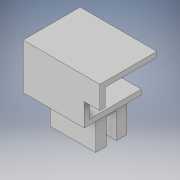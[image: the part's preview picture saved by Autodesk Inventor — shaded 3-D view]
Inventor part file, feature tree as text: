
AUTODESK INVENTOR PART (.ipt)
format: ipt  version: 2019 (Build 230136000, 136)  size: 295,424 bytes
history: native  units: in
note: dims shown in document units (in); Inventor stores cm internally (conversion verified against a paired STEP export)
features: extrude x4, sketch x4, projected_geometry x1
ambient origin geometry x8: Origin, YZ Plane, XZ Plane, XY Plane, X Axis, Y Axis, Z Axis, Center Point
bodies: Body1 (feature_tree)
feature tree (9):
  extrude  "Extrusion2"  Depth=0.2165in
  extrude  "Extrusion4"  Depth=0.0984in
  extrude  "Extrusion9"  Depth=0.8661in
  extrude  "Extrusion10"  Depth=0.5906in
  sketch  "Sketch4"  dims[d32=0.7677in d33=0.0984in]
  projected_geometry  "Projected Loop1"
  sketch  "Sketch9"  dims[d34=0.0984in d35=0.8661in]
  sketch  "Sketch10"  dims[d36=0.7874in d37=0.0in d38=0.5906in d58=0.0984in d59=0.1969in d60=0.0in d61=0.0984in d62=0.0in d63=0.2953in d64=0.0in d65=1.4567in d66=1.3583in d67=0.0984in]
  sketch  "Sketch2"  dims[d8=0.5906in d9=0.5906in d10=0.1969in d11=0.4921in d12=0.1969in d14=0.0in d15=0.8661in d29=0.2165in]
